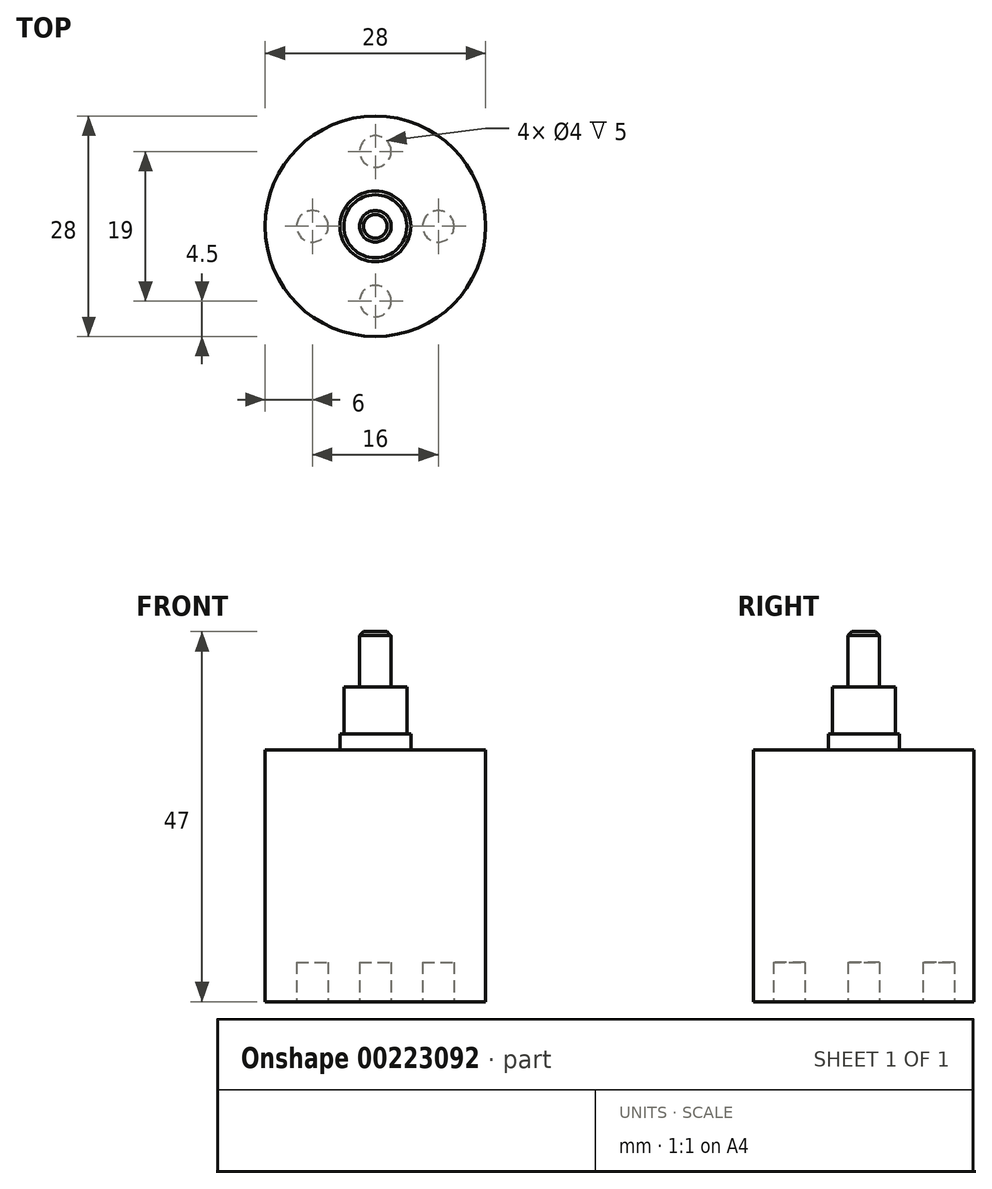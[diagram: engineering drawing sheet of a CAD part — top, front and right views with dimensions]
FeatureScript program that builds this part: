
annotation { "Feature Type Name" : "Feature", "Feature Type Description" : "" }
export const myFeature = defineFeature(function(context is Context, id is Id, definition is map)
    precondition{}
    {
        {
            var Q0;
            Q0=qCreatedBy(makeId("Top.planeOp"),FACE);
            var sketch = newSketch(context, id + "F0", { "sketchPlane" : qUnion([Q0])});
            skCircle(sketch, "E0", {"center": v(0, 0) * mm, "radius": 14 * mm});
            skSolve(sketch);
        }
        {
            var Q0;
            Q0=makeQuery(id+"F0.imprint","IMPRINT",FACE,{"disambiguationData":[TD([[makeQuery(id+"F0.imprint","IMPRINT",EDGE,{"derivedFrom":sQuery(id+"F0.wireOp",EDGE,"E0")}),1.0]])]});
            extrude(context, id + "F1", {"entities" : qUnion([Q0]), "depth" : 32 * mm});
        }
        {
            var Q0;
            Q0=makeQuery(id+"F1.opExtrude","CAP_FACE",FACE,{"disambiguationData":[OSD([sQuery(id+"F0.wireOp",EDGE,"E0")])],"isStart":false});
            var sketch = newSketch(context, id + "F2", { "sketchPlane" : qUnion([Q0])});
            skCircle(sketch, "E1.0", {"center": v(0, 0) * mm, "radius": 14 * mm, "construction": true});
            skCircle(sketch, "E2", {"center": v(0, 0) * mm, "radius": 4.5 * mm});
            skSolve(sketch);
        }
        {
            var Q0;
            Q0=makeQuery(id+"F2.imprint","IMPRINT",FACE,{"disambiguationData":[TD([[makeQuery(id+"F2.imprint","IMPRINT",EDGE,{"derivedFrom":sQuery(id+"F2.wireOp",EDGE,"E2")}),1.0]])]});
            extrude(context, id + "F3", {"entities" : qUnion([Q0]), "operationType" : NewBodyOperationType.ADD, "depth" : 2 * mm});
        }
        {
            var Q0;
            Q0=makeQuery(id+"F3.opExtrude","CAP_FACE",FACE,{"disambiguationData":[OSD([sQuery(id+"F2.wireOp",EDGE,"E2")])],"isStart":false});
            var sketch = newSketch(context, id + "F4", { "sketchPlane" : qUnion([Q0])});
            skCircle(sketch, "E3.0.0", {"center": v(0, 0) * mm, "radius": 4.5 * mm, "construction": true});
            skCircle(sketch, "E4", {"center": v(0, 0) * mm, "radius": 2 * mm});
            skSolve(sketch);
        }
        {
            var Q0;
            Q0=makeQuery(id+"F4.imprint","IMPRINT",FACE,{"disambiguationData":[TD([[makeQuery(id+"F4.imprint","IMPRINT",EDGE,{"derivedFrom":sQuery(id+"F4.wireOp",EDGE,"E4")}),1.0]])]});
            extrude(context, id + "F5", {"entities" : qUnion([Q0]), "operationType" : NewBodyOperationType.ADD, "depth" : 13 * mm});
        }
        {
            var Q0;
            Q0=makeQuery(id+"F5.opExtrude","CAP_EDGE",EDGE,{"disambiguationData":[OSD([sQuery(id+"F4.wireOp",EDGE,"E4")])],"isStart":false});
            chamfer(context, id + "F6", {"entities" : qUnion([Q0]), "width" : .5 * mm, "tangentPropagation" : true});
        }
        {
            var Q0;
            Q0=makeQuery(id+"F1.opExtrude","CAP_FACE",FACE,{"disambiguationData":[OSD([sQuery(id+"F0.wireOp",EDGE,"E0")])],"isStart":true});
            var sketch = newSketch(context, id + "F7", { "sketchPlane" : qUnion([Q0])});
            skCircle(sketch, "E5", {"center": v(-8, 0) * mm, "radius": 2 * mm});
            skCircle(sketch, "E6", {"center": v(8, 0) * mm, "radius": 2 * mm});
            skCircle(sketch, "E7", {"center": v(0, 9.5) * mm, "radius": 2 * mm});
            skCircle(sketch, "E8", {"center": v(0, -9.5) * mm, "radius": 2 * mm});
            skLineSegment(sketch, "E9", {"start": v(-8, 0) * mm, "end": v(0, 0) * mm, "construction": true});
            skLineSegment(sketch, "E10", {"start": v(0, 0) * mm, "end": v(8, 0) * mm, "construction": true});
            skLineSegment(sketch, "E11", {"start": v(0, -9.5) * mm, "end": v(0, 0) * mm, "construction": true});
            skLineSegment(sketch, "E12", {"start": v(0, 0) * mm, "end": v(0, 9.5) * mm, "construction": true});
            skSolve(sketch);
        }
        {
            var Q0;
            Q0 = qSketchRegion(id + "F7", true);
            extrude(context, id + "F8", {"entities" : qUnion([Q0]), "operationType" : NewBodyOperationType.REMOVE, "oppositeDirection" : true, "depth" : 5 * mm});
        }
        {
            var Q0;
            Q0=makeQuery(id+"F3.opExtrude","CAP_FACE",FACE,{"disambiguationData":[OSD([sQuery(id+"F2.wireOp",EDGE,"E2")])],"isStart":false});
            var sketch = newSketch(context, id + "F9", { "sketchPlane" : qUnion([Q0])});
            skSolve(sketch);
        }
        {
            var Q0;
            Q0=makeQuery(id+"F9.imprint","IMPRINT",FACE,{"disambiguationData":[TD([[makeQuery(id+"F9.imprint","IMPRINT",EDGE,{"derivedFrom":makeQuery(id+"F3.opExtrude","CAP_EDGE",EDGE,{"disambiguationData":[OSD([sQuery(id+"F2.wireOp",EDGE,"E2")])],"isStart":false})}),1.0]])]});
            var sketch = newSketch(context, id + "F10", { "sketchPlane" : qUnion([Q0])});
            skCircle(sketch, "E13", {"center": v(0, 0) * mm, "radius": 4 * mm});
            skSolve(sketch);
        }
        {
            var Q0;
            Q0 = qSketchRegion(id + "F10", true);
            extrude(context, id + "F11", {"entities" : qUnion([Q0]), "operationType" : NewBodyOperationType.ADD, "depth" : 6 * mm});
        }
    });
